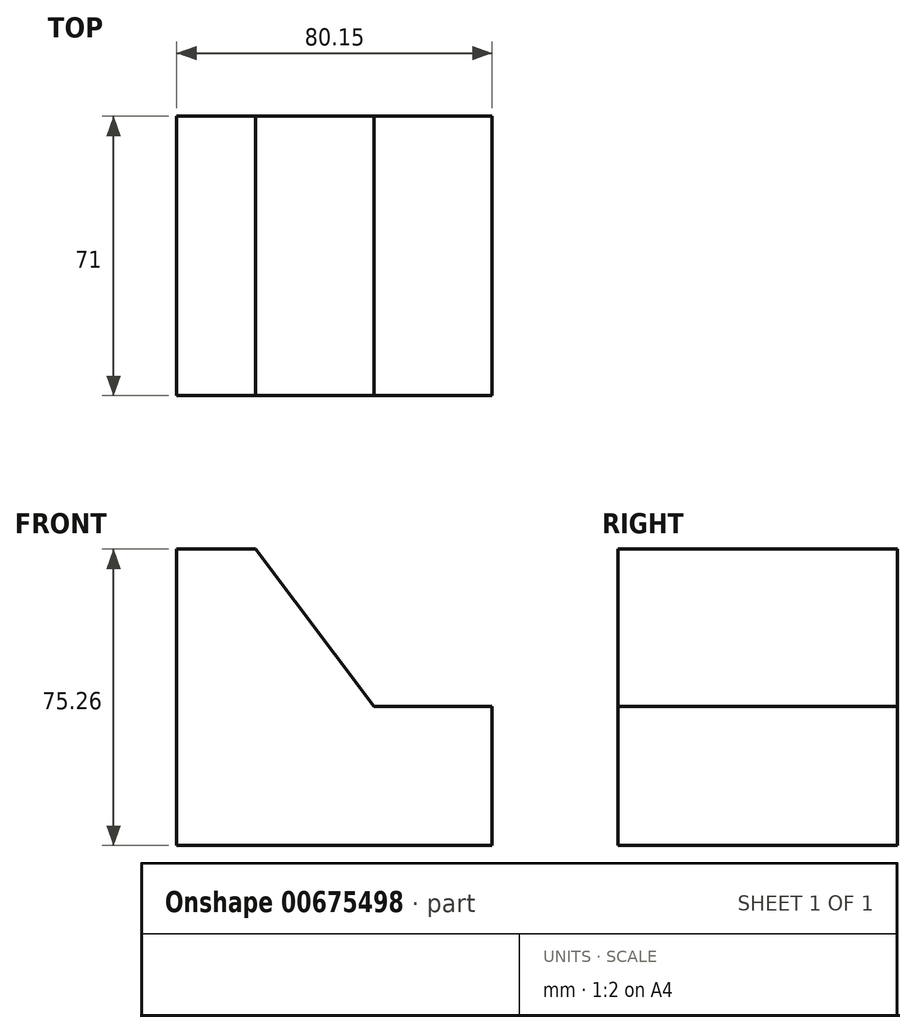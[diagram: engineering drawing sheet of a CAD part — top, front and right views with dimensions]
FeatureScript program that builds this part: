
annotation { "Feature Type Name" : "Feature", "Feature Type Description" : "" }
export const myFeature = defineFeature(function(context is Context, id is Id, definition is map)
    precondition{}
    {
        {
            var Q0;
            Q0=qCreatedBy(makeId("Front.planeOp"),FACE);
            var sketch = newSketch(context, id + "F0", { "sketchPlane" : qUnion([Q0])});
            skLineSegment(sketch, "E0", {"start": v(0, 0) * mm, "end": v(20, 0) * mm});
            skLineSegment(sketch, "E1", {"start": v(20, 0) * mm, "end": v(50.14, -40) * mm});
            skLineSegment(sketch, "E2", {"start": v(50.14, -40) * mm, "end": v(80.15, -40) * mm});
            skLineSegment(sketch, "E3", {"start": v(80.15, -40) * mm, "end": v(80.15, -75.26) * mm});
            skLineSegment(sketch, "E4", {"start": v(80.15, -75.26) * mm, "end": v(0, -75.26) * mm});
            skLineSegment(sketch, "E5", {"start": v(0, -75.26) * mm, "end": v(0, 0) * mm});
            skSolve(sketch);
        }
        {
            var Q0;
            Q0 = qSketchRegion(id + "F0", true);
            extrude(context, id + "F1", {"entities" : qUnion([Q0]), "oppositeDirection" : true, "depth" : 71 * mm, "offsetDistance" : 25 * mm});
        }
    });
